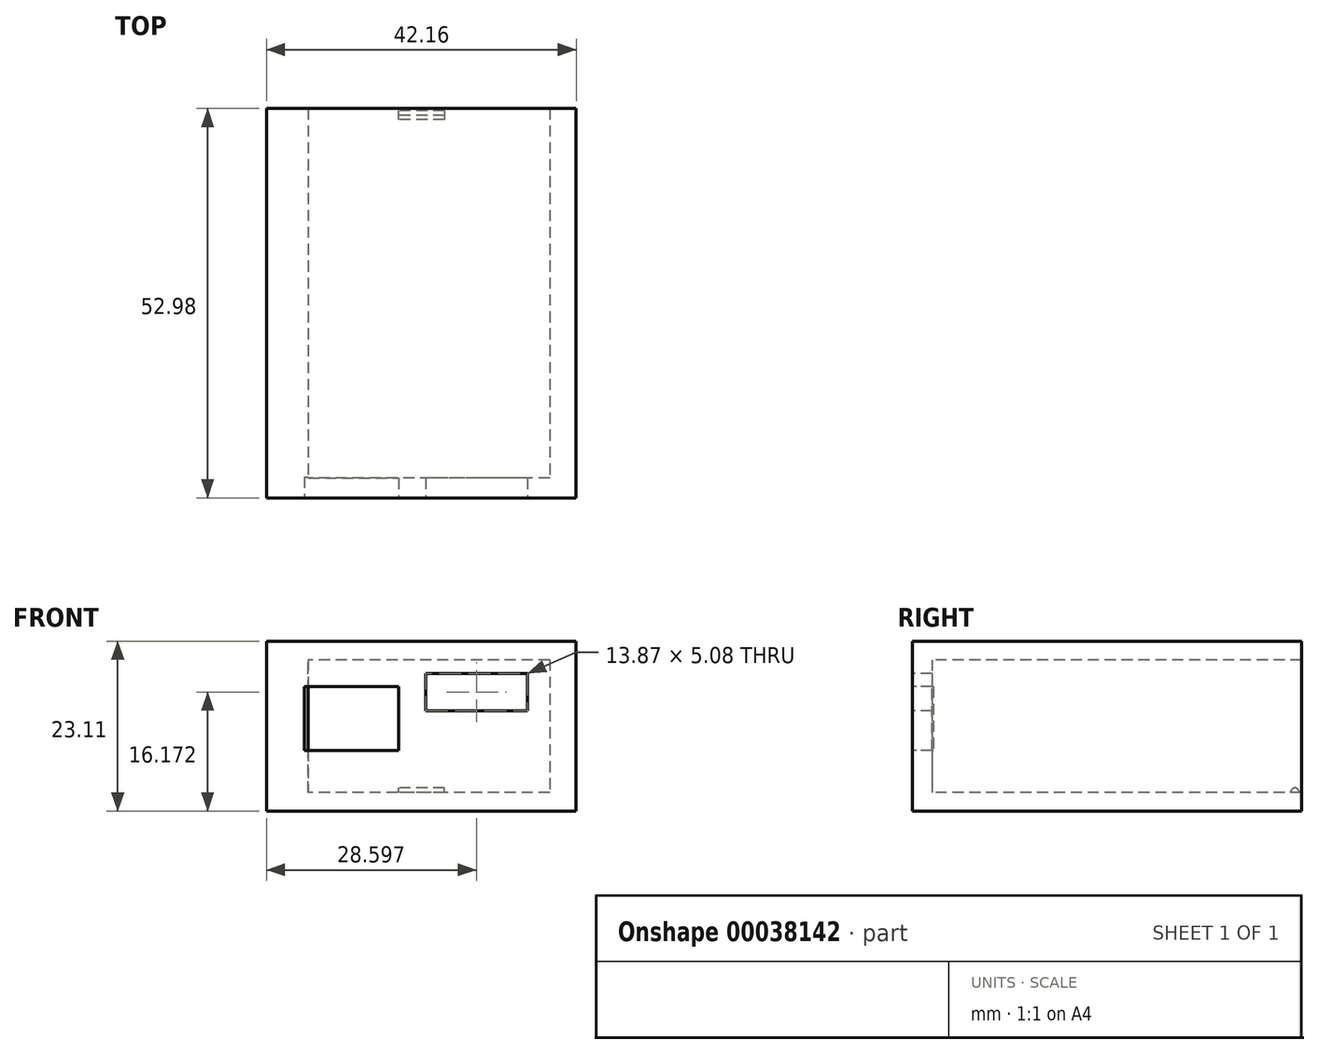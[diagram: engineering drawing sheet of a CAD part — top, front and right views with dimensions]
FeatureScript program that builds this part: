
annotation { "Feature Type Name" : "Feature", "Feature Type Description" : "" }
export const myFeature = defineFeature(function(context is Context, id is Id, definition is map)
    precondition{}
    {
        {
            var Q0;
            Q0=qCreatedBy(makeId("Top.planeOp"),FACE);
            var sketch = newSketch(context, id + "F0", { "sketchPlane" : qUnion([Q0])});
            skLineSegment(sketch, "E0.rect.bottom", {"start": v(17.46, 23.81) * mm, "end": v(-17.46, 23.81) * mm});
            skLineSegment(sketch, "E0.rect.top", {"start": v(17.46, -23.81) * mm, "end": v(-17.46, -23.81) * mm});
            skLineSegment(sketch, "E0.rect.left", {"start": v(17.46, 23.81) * mm, "end": v(17.46, -23.81) * mm});
            skLineSegment(sketch, "E0.rect.right", {"start": v(-17.46, 23.81) * mm, "end": v(-17.46, -23.81) * mm});
            skPoint(sketch, "E0.rect.middle", {"position": v(0, 0) * mm});
            skLineSegment(sketch, "E1.rect.bottom", {"start": v(21.08, 26.49) * mm, "end": v(-21.08, 26.49) * mm});
            skLineSegment(sketch, "E1.rect.top", {"start": v(21.08, -26.49) * mm, "end": v(-21.08, -26.49) * mm});
            skLineSegment(sketch, "E1.rect.left", {"start": v(21.08, 26.49) * mm, "end": v(21.08, -26.49) * mm});
            skLineSegment(sketch, "E1.rect.right", {"start": v(-21.08, 26.49) * mm, "end": v(-21.08, -26.49) * mm});
            skSolve(sketch);
        }
        {
            var Q0;
            Q0=makeQuery(id+"F0.imprint","IMPRINT",FACE,{"disambiguationData":[TD([[makeQuery(id+"F0.imprint","IMPRINT",EDGE,{"derivedFrom":sQuery(id+"F0.wireOp",EDGE,"E0.rect.bottom")}),-1.0]])]});
            extrude(context, id + "F1", {"entities" : qUnion([Q0]), "depth" : 18.03 * mm});
        }
        {
            var Q0;
            Q0=makeQuery(id+"F0.imprint","IMPRINT",FACE,{"disambiguationData":[TD([[makeQuery(id+"F0.imprint","IMPRINT",EDGE,{"derivedFrom":sQuery(id+"F0.wireOp",EDGE,"E0.rect.bottom")}),1.0]])]});
            var Q1;
            Q1=makeQuery(id+"F0.imprint","IMPRINT",FACE,{"disambiguationData":[TD([[makeQuery(id+"F0.imprint","IMPRINT",EDGE,{"derivedFrom":sQuery(id+"F0.wireOp",EDGE,"E0.rect.bottom")}),-1.0]])]});
            extrude(context, id + "F2", {"entities" : qUnion([Q0, Q1]), "operationType" : NewBodyOperationType.ADD, "oppositeDirection" : true, "depth" : 2.54 * mm});
        }
        {
            var Q0;
            Q0=makeQuery(id+"F1.opExtrude","SWEPT_FACE",FACE,{"disambiguationData":[OSD([sQuery(id+"F0.wireOp",EDGE,"E0.rect.bottom")])]});
            var sketch = newSketch(context, id + "F3", { "sketchPlane" : qUnion([Q0])});
            skLineSegment(sketch, "E2.bottom", {"start": v(17.46, 18.03) * mm, "end": v(-17.46, 18.03) * mm});
            skLineSegment(sketch, "E2.top", {"start": v(17.46, 0) * mm, "end": v(-17.46, 0) * mm});
            skLineSegment(sketch, "E2.left", {"start": v(17.46, 18.03) * mm, "end": v(17.46, 0) * mm});
            skLineSegment(sketch, "E2.right", {"start": v(-17.46, 18.03) * mm, "end": v(-17.46, 0) * mm});
            skSolve(sketch);
        }
        {
            var Q0;
            Q0 = qSketchRegion(id + "F3", true);
            var Q1;
            {var subQ0=sQuery(id+"F0.wireOp",EDGE,"E1.rect.bottom");Q1=makeQuery(id+"F2.boolean.opBoolean","MERGE",FACE,{"derivedFrom":[makeQuery(id+"F1.opExtrude","SWEPT_FACE",FACE,{"disambiguationData":[OSD([subQ0])]}),makeQuery(id+"F2.opExtrude","SWEPT_FACE",FACE,{"disambiguationData":[OSD([subQ0])]})]});}
            extrude(context, id + "F4", {"entities" : qUnion([Q0, Q1]), "operationType" : NewBodyOperationType.REMOVE, "oppositeDirection" : true, "depth" : 10.33 * mm});
        }
        {
            var Q0;
            Q0=makeQuery(id+"F1.opExtrude","CAP_FACE",FACE,{"disambiguationData":[OSD([sQuery(id+"F0.wireOp",EDGE,"E0.rect.bottom"),sQuery(id+"F0.wireOp",EDGE,"E0.rect.top"),sQuery(id+"F0.wireOp",EDGE,"E0.rect.left"),sQuery(id+"F0.wireOp",EDGE,"E0.rect.right"),sQuery(id+"F0.wireOp",EDGE,"E1.rect.bottom"),sQuery(id+"F0.wireOp",EDGE,"E1.rect.top"),sQuery(id+"F0.wireOp",EDGE,"E1.rect.left"),sQuery(id+"F0.wireOp",EDGE,"E1.rect.right")])],"isStart":false});
            var sketch = newSketch(context, id + "F5", { "sketchPlane" : qUnion([Q0])});
            skLineSegment(sketch, "E3.bottom", {"start": v(-21.08, 26.49) * mm, "end": v(21.08, 26.49) * mm});
            skLineSegment(sketch, "E3.top", {"start": v(-21.08, -26.49) * mm, "end": v(21.08, -26.49) * mm});
            skLineSegment(sketch, "E3.left", {"start": v(-21.08, 26.49) * mm, "end": v(-21.08, -26.49) * mm});
            skLineSegment(sketch, "E3.right", {"start": v(21.08, 26.49) * mm, "end": v(21.08, -26.49) * mm});
            skSolve(sketch);
        }
        {
            var Q0;
            Q0 = qSketchRegion(id + "F5", true);
            extrude(context, id + "F6", {"entities" : qUnion([Q0]), "operationType" : NewBodyOperationType.ADD, "depth" : 2.54 * mm});
        }
        {
            var Q0;
            {var subQ0=sQuery(id+"F0.wireOp",EDGE,"E1.rect.top");Q0=makeQuery(id+"F6.boolean.opBoolean","MERGE",FACE,{"derivedFrom":[makeQuery(id+"F2.boolean.opBoolean","MERGE",FACE,{"derivedFrom":[makeQuery(id+"F1.opExtrude","SWEPT_FACE",FACE,{"disambiguationData":[OSD([subQ0])]}),makeQuery(id+"F2.opExtrude","SWEPT_FACE",FACE,{"disambiguationData":[OSD([subQ0])]})]}),makeQuery(id+"F6.opExtrude","SWEPT_FACE",FACE,{"disambiguationData":[OSD([sQuery(id+"F5.wireOp",EDGE,"E3.top")])]})]});}
            var sketch = newSketch(context, id + "F7", { "sketchPlane" : qUnion([Q0])});
            skLineSegment(sketch, "E4.bottom", {"start": v(14.45, 16.17) * mm, "end": v(0.58, 16.17) * mm});
            skLineSegment(sketch, "E4.top", {"start": v(14.45, 11.09) * mm, "end": v(0.58, 11.09) * mm});
            skLineSegment(sketch, "E4.left", {"start": v(14.45, 16.17) * mm, "end": v(14.45, 11.09) * mm});
            skLineSegment(sketch, "E4.right", {"start": v(0.58, 16.17) * mm, "end": v(0.58, 11.09) * mm});
            skSolve(sketch);
        }
        {
            var Q0;
            {var subQ0=sQuery(id+"F7.wireOp",EDGE,"E4.bottom");Q0=makeQuery(id+"F7.imprint","IMPRINT",FACE,{"disambiguationData":[TD([[makeQuery(id+"F7.imprint","IMPRINT",EDGE,{"derivedFrom":subQ0}),1.0]])]});}
            extrude(context, id + "F8", {"entities" : qUnion([Q0]), "operationType" : NewBodyOperationType.REMOVE, "oppositeDirection" : true, "depth" : 25.4 * mm});
        }
        {
            var Q0;
            Q0=makeQuery(id+"F0.imprint","IMPRINT",FACE,{"disambiguationData":[TD([[makeQuery(id+"F0.imprint","IMPRINT",EDGE,{"derivedFrom":sQuery(id+"F0.wireOp",EDGE,"E0.rect.bottom")}),1.0]])]});
            var sketch = newSketch(context, id + "F9", { "sketchPlane" : qUnion([Q0])});
            skLineSegment(sketch, "E5.rect.bottom", {"start": v(3.13, 26.2) * mm, "end": v(-3.13, 26.2) * mm});
            skLineSegment(sketch, "E5.rect.top", {"start": v(3.13, 24.95) * mm, "end": v(-3.13, 24.95) * mm});
            skLineSegment(sketch, "E5.rect.left", {"start": v(3.13, 26.2) * mm, "end": v(3.13, 24.95) * mm});
            skLineSegment(sketch, "E5.rect.right", {"start": v(-3.13, 26.2) * mm, "end": v(-3.13, 24.95) * mm});
            skPoint(sketch, "E5.rect.middle", {"position": v(0, 25.58) * mm});
            skSolve(sketch);
        }
        {
            var Q0;
            Q0=makeQuery(id+"F9.imprint","IMPRINT",FACE,{"disambiguationData":[TD([[makeQuery(id+"F9.imprint","IMPRINT",EDGE,{"derivedFrom":sQuery(id+"F9.wireOp",EDGE,"E5.rect.bottom")}),1.0]])]});
            var Q1;
            Q1=sQuery(id+"F9.wireOp",EDGE,"E5.rect.bottom");
            var Q2;
            Q2=sQuery(id+"F9.wireOp",EDGE,"E5.rect.right");
            var Q3;
            Q3=sQuery(id+"F9.wireOp",EDGE,"E5.rect.top");
            var Q4;
            Q4=sQuery(id+"F9.wireOp",EDGE,"E5.rect.left");
            extrude(context, id + "F10", {"entities" : qUnion([Q0]), "operationType" : NewBodyOperationType.ADD, "surfaceEntities" : qUnion([Q1, Q2, Q3, Q4]), "depth" : 0.64 * mm});
        }
        {
            var Q0;
            Q0=makeQuery(id+"F10.opExtrude","CAP_EDGE",EDGE,{"disambiguationData":[OSD([sQuery(id+"F9.wireOp",EDGE,"E5.rect.bottom")])],"isStart":false});
            var Q1;
            Q1=makeQuery(id+"F10.opExtrude","CAP_EDGE",EDGE,{"disambiguationData":[OSD([sQuery(id+"F9.wireOp",EDGE,"E5.rect.top")])],"isStart":false});
            fillet(context, id + "F11", {"entities" : qUnion([Q0, Q1]), "radius" : 0.82 * mm, "tangentPropagation" : true, "allowEdgeOverflow" : false});
        }
        {
            var Q0;
            Q0=makeQuery(id+"F4.boolean.opBoolean","MERGE",FACE,{"derivedFrom":[makeQuery(id+"F1.opExtrude","SWEPT_FACE",FACE,{"disambiguationData":[OSD([sQuery(id+"F0.wireOp",EDGE,"E0.rect.right")])]}),makeQuery(id+"F4.opExtrude","SWEPT_FACE",FACE,{"disambiguationData":[OSD([sQuery(id+"F3.wireOp",EDGE,"E2.right")])]})]});
            extrude(context, id + "F12", {"entities" : qUnion([Q0]), "operationType" : NewBodyOperationType.ADD, "depth" : 2.1 * mm});
        }
        {
            var Q0;
            {var subQ0=sQuery(id+"F0.wireOp",EDGE,"E1.rect.top");Q0=makeQuery(id+"F6.boolean.opBoolean","MERGE",FACE,{"derivedFrom":[makeQuery(id+"F2.boolean.opBoolean","MERGE",FACE,{"derivedFrom":[makeQuery(id+"F1.opExtrude","SWEPT_FACE",FACE,{"disambiguationData":[OSD([subQ0])]}),makeQuery(id+"F2.opExtrude","SWEPT_FACE",FACE,{"disambiguationData":[OSD([subQ0])]})]}),makeQuery(id+"F6.opExtrude","SWEPT_FACE",FACE,{"disambiguationData":[OSD([sQuery(id+"F5.wireOp",EDGE,"E3.top")])]})]});}
            var sketch = newSketch(context, id + "F13", { "sketchPlane" : qUnion([Q0])});
            skLineSegment(sketch, "E6.bottom", {"start": v(-15.9, 5.72) * mm, "end": v(-3.11, 5.72) * mm});
            skLineSegment(sketch, "E6.top", {"start": v(-15.9, 14.36) * mm, "end": v(-3.11, 14.36) * mm});
            skLineSegment(sketch, "E6.left", {"start": v(-15.9, 5.72) * mm, "end": v(-15.9, 14.36) * mm});
            skLineSegment(sketch, "E6.right", {"start": v(-3.11, 5.72) * mm, "end": v(-3.11, 14.36) * mm});
            skSolve(sketch);
        }
        {
            var Q0;
            Q0=makeQuery(id+"F13.imprint","IMPRINT",FACE,{"disambiguationData":[TD([[makeQuery(id+"F13.imprint","IMPRINT",EDGE,{"derivedFrom":sQuery(id+"F13.wireOp",EDGE,"E6.bottom")}),1.0]])]});
            extrude(context, id + "F14", {"entities" : qUnion([Q0]), "operationType" : NewBodyOperationType.REMOVE, "oppositeDirection" : true, "depth" : 2.85 * mm});
        }
    });
